# Revit family: 318_9a689d3108a543b69a2137953e2806
name_source: partatom
category: Pipe Accessories
revit_build: Autodesk Revit 2017 (Build: 20160225_1515(x64)
units: mm (PartAtom-declared; Revit-internal decimal feet)

## family parameters
Always vertical = Yes
Cut with Voids When Loaded = No
Part Type = Valve - Normal
Round Connector Dimension = Use Diameter
Shared = No
Work Plane-Based = No

## types (1)
- R559NY010
    CAT0 = Yes
    D2 = 44 mm  [stored 0.144357 ft]
    D31 = 18 mm  [stored 0.0590551 ft]
    D32 = 14 mm  [stored 0.0459318 ft]
    D4 = 22 mm  [stored 0.0721785 ft]
    Description = MANIFOLD WITH MIXING VALVE AND ELECTRONIC REGULATION
    E = 285 mm  [stored 0.935039 ft]
    H11 = 10 mm  [stored 0.0328084 ft]
    H12 = 30 mm  [stored 0.0984252 ft]
    H2 = 20 mm  [stored 0.0656168 ft]
    H2__ve = -20 mm  [stored -0.0656168 ft]
    H3 = 40 mm  [stored 0.131234 ft]
    H3__ve = -40 mm  [stored -0.131234 ft]
    H4 = 5 mm  [stored 0.0164042 ft]
    H5 = 33 mm  [stored 0.108268 ft]
    I = 50 mm  [stored 0.164042 ft]
    L = 500 mm  [stored 1.64042 ft]
    MC_Default_elevation = 0 mm  [stored 0 ft]
    Manufacturer = Giacomini
    N10 = Yes
    N11 = No
    N12 = No
    N5 = Yes
    N6 = Yes
    N7 = Yes
    N8 = Yes
    N9 = Yes
    QmdConnectorList = 321;SMP;322;SBP1;323;SBP2;324;SBP3;325;SBP4;326;SBP5;327;SBP6;328;SBP7;329;SBP8;330;SBP9;331;SBP10;351;RMP;352;RBP1;353;RBP2;354;RBP3;355;RBP4;356;RBP5;357;RBP6;358;RBP7;359;RBP8;360;RBP9;361;RBP10
    R2 = 22 mm  [stored 0.0721785 ft]
    RBP1 = 18 mm
    RBP10 = 18 mm
    RBP11 = 18 mm  [stored 0.0590551 ft]
    RBP12 = 18 mm  [stored 0.0590551 ft]
    RBP2 = 18 mm
    RBP3 = 18 mm
    RBP4 = 18 mm
    RBP5 = 18 mm
    RBP6 = 18 mm
    RBP7 = 18 mm
    RBP8 = 18 mm
    RBP9 = 18 mm
    RMP = 25 mm
    SBP1 = 18 mm
    SBP10 = 18 mm
    SBP11 = 18 mm  [stored 0.0590551 ft]
    SBP12 = 18 mm  [stored 0.0590551 ft]
    SBP2 = 18 mm
    SBP3 = 18 mm
    SBP4 = 18 mm
    SBP5 = 18 mm
    SBP6 = 18 mm
    SBP7 = 18 mm
    SBP8 = 18 mm
    SBP9 = 18 mm
    SMP = 25 mm
    URL = http://www.giacomini.com
    VL1 = 287 mm  [stored 0.941601 ft]
    X1 = 312 mm  [stored 1.02362 ft]
    magiPartTypeId = 318
    magiProductCode = R559NY010
    magiProductFamilyId = 9a689d3108a543b69a2137953e2806
    magiProductId = 9a689d3108a543b69a2137953e2806

note: [stored X ft] marks values corroborated as IEEE doubles in the binary element streams (Revit-internal decimal feet)

## geometry (parser evidence)
native form markers: Sweep x3
no freeform markers — native parametric forms only
